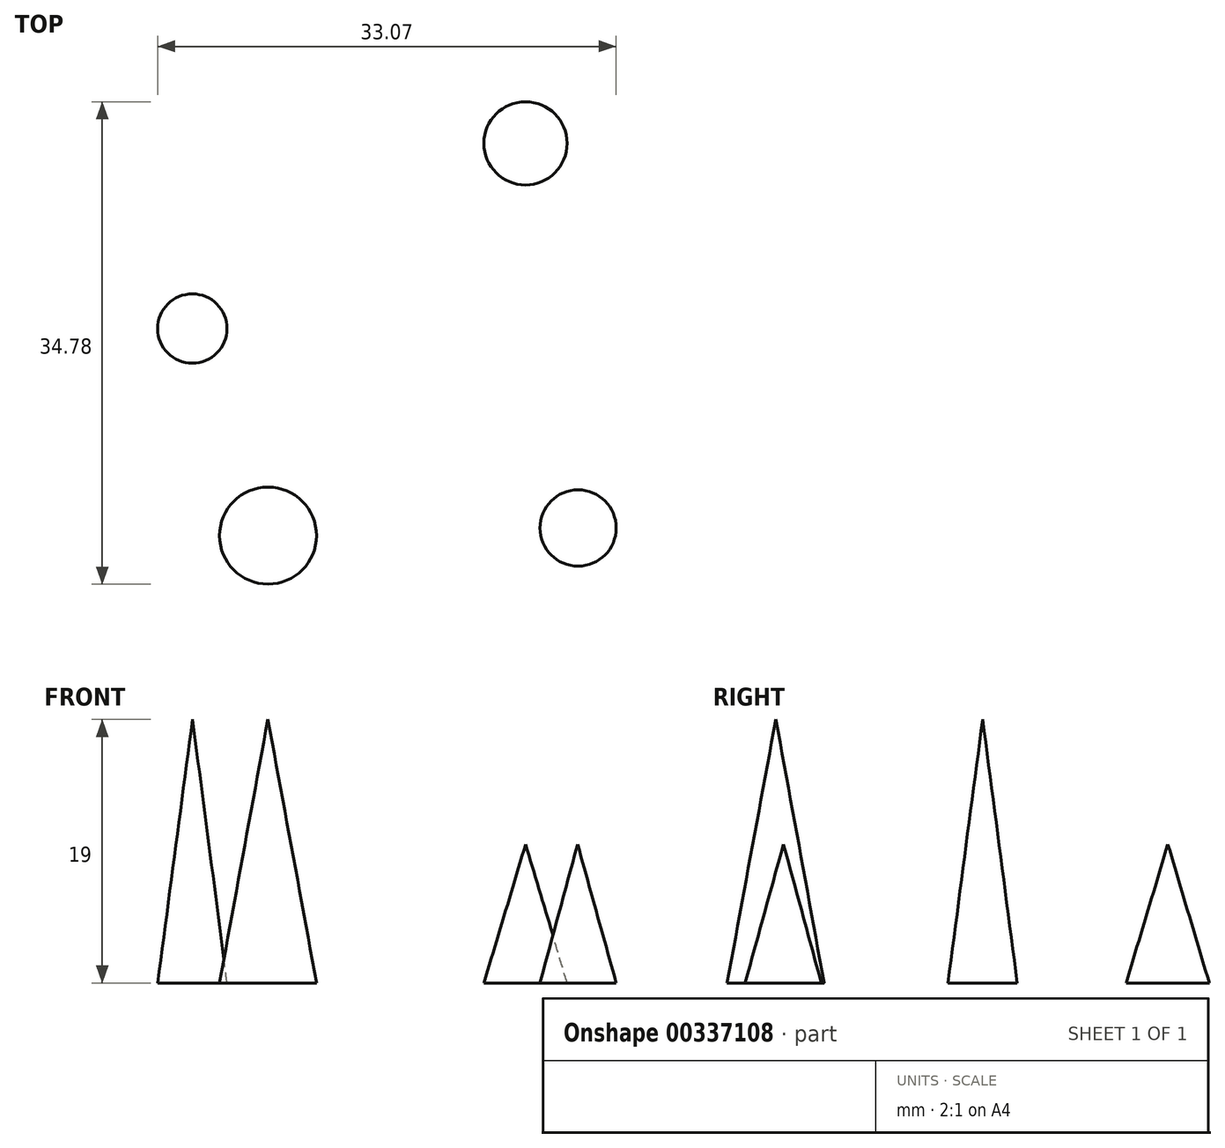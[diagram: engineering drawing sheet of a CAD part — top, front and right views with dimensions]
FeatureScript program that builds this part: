
annotation { "Feature Type Name" : "Feature", "Feature Type Description" : "" }
export const myFeature = defineFeature(function(context is Context, id is Id, definition is map)
    precondition{}
    {
        {
            var Q0;
            Q0=qCreatedBy(makeId("Top.planeOp"),FACE);
            var sketch = newSketch(context, id + "F0", { "sketchPlane" : qUnion([Q0])});
            skCircle(sketch, "E0", {"center": v(-50.3, 31.37) * mm, "radius": 2.5 * mm});
            skCircle(sketch, "E1", {"center": v(-26.28, 44.72) * mm, "radius": 3 * mm});
            skCircle(sketch, "E2", {"center": v(-22.49, 16.99) * mm, "radius": 2.75 * mm});
            skCircle(sketch, "E3", {"center": v(-44.85, 16.44) * mm, "radius": 3.5 * mm});
            skSolve(sketch);
        }
        {
            var Q0;
            Q0=qCreatedBy(makeId("Top.planeOp"),FACE);
            cPlane(context, id + "F1", {"entities" : qUnion([Q0]), "cplaneType" : CPlaneType.OFFSET, "offset" : 19 * mm, "width" : 150 * mm, "height" : 150 * mm});
        }
        {
            var Q0;
            Q0=qCreatedBy(id+"F1.planeOp",FACE);
            var sketch = newSketch(context, id + "F2", { "sketchPlane" : qUnion([Q0])});
            skPoint(sketch, "E4", {"position": v(-44.86, 16.46) * mm});
            skPoint(sketch, "E5", {"position": v(-50.3, 31.37) * mm});
            skSolve(sketch);
        }
        {
            var Q0;
            Q0=makeQuery(id+"F0.imprint","IMPRINT",FACE,{"disambiguationData":[TD([[makeQuery(id+"F0.imprint","IMPRINT",EDGE,{"derivedFrom":sQuery(id+"F0.wireOp",EDGE,"E3")}),1.0]])]});
            var Q1;
            Q1=sQuery(id+"F2.wireOp",VERTEX,"E4");
            loft(context, id + "F3", {"sheetProfilesArray" : [{ "sheetProfileEntities" : qUnion([Q0]) }, { "sheetProfileEntities" : qUnion([Q1]) }]});
        }
        {
            var Q0;
            Q0=makeQuery(id+"F0.imprint","IMPRINT",FACE,{"disambiguationData":[TD([[makeQuery(id+"F0.imprint","IMPRINT",EDGE,{"derivedFrom":sQuery(id+"F0.wireOp",EDGE,"E0")}),1.0]])]});
            var Q1;
            Q1=sQuery(id+"F2.wireOp",VERTEX,"E5");
            loft(context, id + "F4", {"sheetProfilesArray" : [{ "sheetProfileEntities" : qUnion([Q0]) }, { "sheetProfileEntities" : qUnion([Q1]) }]});
        }
        {
            var Q0;
            Q0=qCreatedBy(makeId("Top.planeOp"),FACE);
            cPlane(context, id + "F5", {"entities" : qUnion([Q0]), "cplaneType" : CPlaneType.OFFSET, "offset" : 10 * mm, "width" : 150 * mm, "height" : 150 * mm});
        }
        {
            var Q0;
            Q0=qCreatedBy(id+"F5.planeOp",FACE);
            var sketch = newSketch(context, id + "F6", { "sketchPlane" : qUnion([Q0])});
            skPoint(sketch, "E6", {"position": v(-26.27, 44.73) * mm});
            skPoint(sketch, "E7", {"position": v(-22.52, 17) * mm});
            skSolve(sketch);
        }
        {
            var Q0;
            Q0=makeQuery(id+"F0.imprint","IMPRINT",FACE,{"disambiguationData":[TD([[makeQuery(id+"F0.imprint","IMPRINT",EDGE,{"derivedFrom":sQuery(id+"F0.wireOp",EDGE,"E2")}),1.0]])]});
            var Q1;
            Q1=sQuery(id+"F6.wireOp",VERTEX,"E7");
            loft(context, id + "F7", {"sheetProfilesArray" : [{ "sheetProfileEntities" : qUnion([Q0]) }, { "sheetProfileEntities" : qUnion([Q1]) }]});
        }
        {
            var Q0;
            Q0=makeQuery(id+"F0.imprint","IMPRINT",FACE,{"disambiguationData":[TD([[makeQuery(id+"F0.imprint","IMPRINT",EDGE,{"derivedFrom":sQuery(id+"F0.wireOp",EDGE,"E1")}),1.0]])]});
            var Q1;
            Q1=sQuery(id+"F6.wireOp",VERTEX,"E6");
            loft(context, id + "F8", {"sheetProfilesArray" : [{ "sheetProfileEntities" : qUnion([Q0]) }, { "sheetProfileEntities" : qUnion([Q1]) }]});
        }
    });
